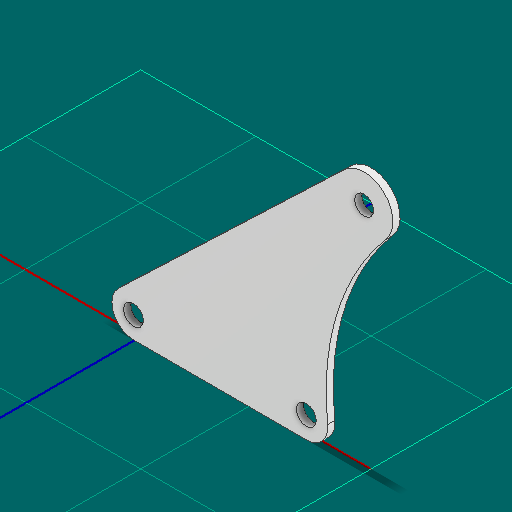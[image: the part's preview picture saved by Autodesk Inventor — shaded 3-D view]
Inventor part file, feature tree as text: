
AUTODESK INVENTOR PART (.ipt)
format: ipt  version: 2025 (Build 290162000, 162)  size: 111,104 bytes
history: native  units: in
note: dims shown in document units (in); Inventor stores cm internally (conversion verified against a paired STEP export)
features: other x3, extrude x1, sketch x1
ambient origin geometry x8: Origin, YZ Plane, XZ Plane, XY Plane, X Axis, Y Axis, Z Axis, Center Point
bodies: Solid1 (feature_tree)
feature tree (5):
  other  "Blocks"
  extrude  "Extrusion1"  Depth=0.0625in TaperAngle=0.0deg
  sketch  "Sketch1"  dims[d0=0.165in d1=2.0in d2=0.5in d3=0.375in d4=0.0625in d5=0.0in]
  other  "main"
  other  "main:1"
